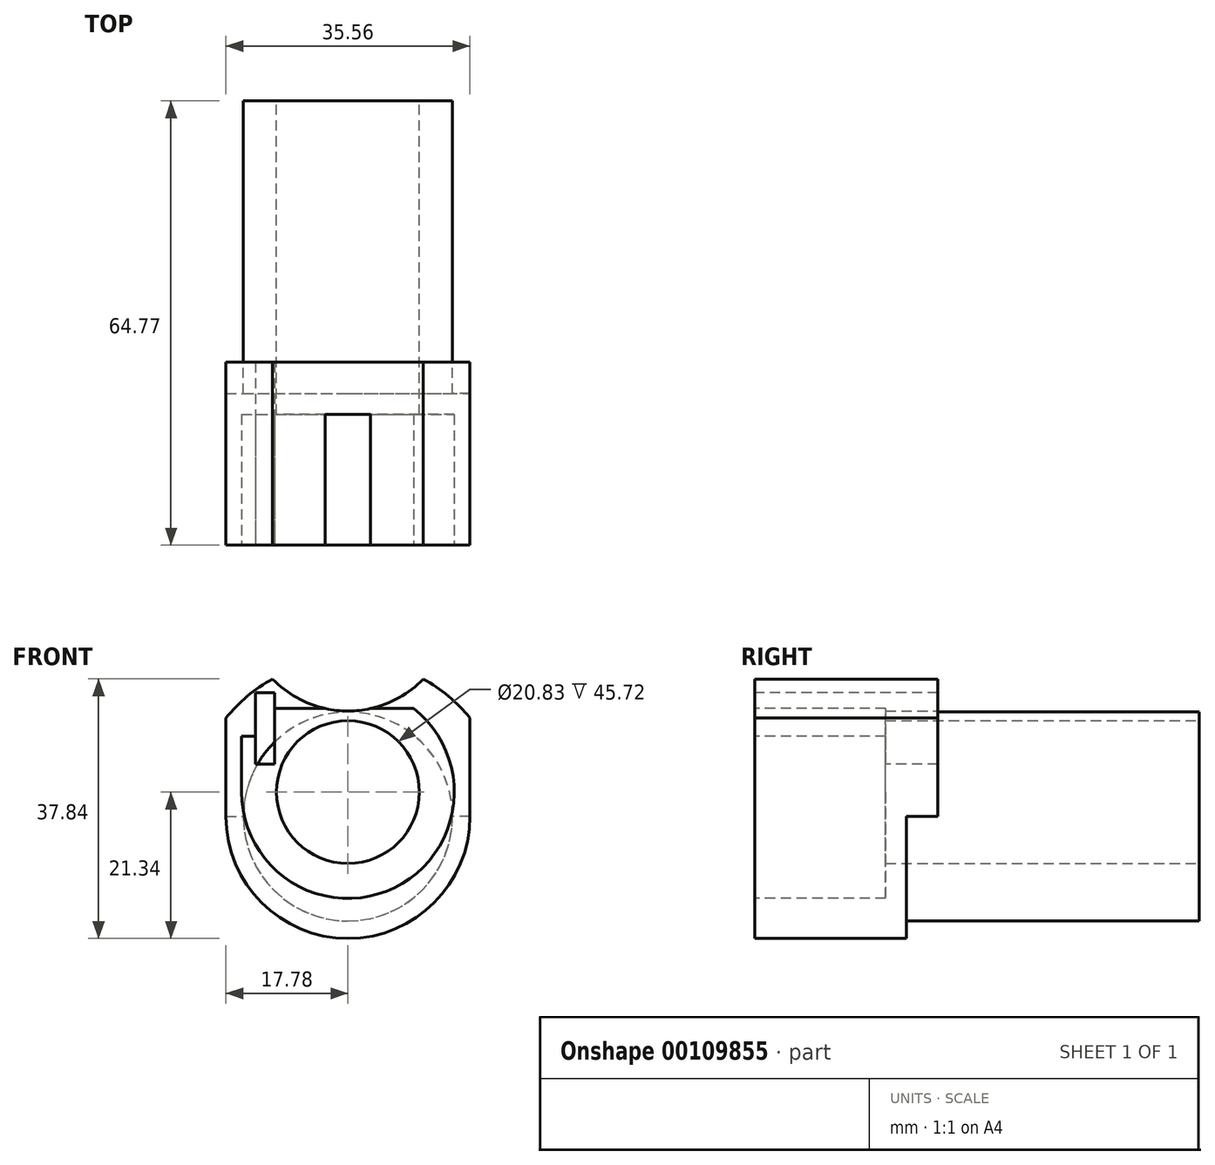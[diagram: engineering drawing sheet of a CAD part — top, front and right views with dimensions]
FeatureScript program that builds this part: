
annotation { "Feature Type Name" : "Feature", "Feature Type Description" : "" }
export const myFeature = defineFeature(function(context is Context, id is Id, definition is map)
    precondition{}
    {
        {
            var Q0;
            Q0=qCreatedBy(makeId("Front.planeOp"),FACE);
            var sketch = newSketch(context, id + "F0", { "sketchPlane" : qUnion([Q0])});
            skCircle(sketch, "E0", {"center": v(0, 0) * mm, "radius": 10.41 * mm});
            skCircle(sketch, "E1", {"center": v(0, -3.56) * mm, "radius": 15.24 * mm});
            skArc(sketch, "E2", {"start": v(-17.78, -3.56) * mm, "mid": v(0, -21.34) * mm, "end": v(17.78, -3.56) * mm});
            skLineSegment(sketch, "E3", {"start": v(-17.78, -3.56) * mm, "end": v(-17.78, 10.81) * mm});
            skLineSegment(sketch, "E4", {"start": v(17.78, 10.81) * mm, "end": v(17.78, -3.56) * mm});
            skArc(sketch, "E5", {"start": v(17.78, 10.81) * mm, "mid": v(14.66, 13.99) * mm, "end": v(10.98, 16.5) * mm});
            skArc(sketch, "E6.trimOffspring", {"start": v(-10.98, 16.5) * mm, "mid": v(-14.66, 13.99) * mm, "end": v(-17.78, 10.81) * mm});
            skArc(sketch, "E7", {"start": v(-10.98, 16.5) * mm, "mid": v(0, 11.83) * mm, "end": v(10.98, 16.5) * mm});
            skSolve(sketch);
        }
        {
            var Q0;
            Q0=makeQuery(id+"F0.imprint","IMPRINT",FACE,{"disambiguationData":[TD([[makeQuery(id+"F0.imprint","IMPRINT",EDGE,{"derivedFrom":sQuery(id+"F0.wireOp",EDGE,"E1")}),-1.0]])]});
            var Q1;
            Q1=makeQuery(id+"F0.imprint","IMPRINT",FACE,{"disambiguationData":[TD([[makeQuery(id+"F0.imprint","IMPRINT",EDGE,{"derivedFrom":sQuery(id+"F0.wireOp",EDGE,"E0")}),-1.0]])]});
            extrude(context, id + "F1", {"entities" : qUnion([Q0, Q1]), "depth" : 26.67 * mm});
        }
        {
            var Q0;
            Q0=makeQuery(id+"F0.imprint","IMPRINT",FACE,{"disambiguationData":[TD([[makeQuery(id+"F0.imprint","IMPRINT",EDGE,{"derivedFrom":sQuery(id+"F0.wireOp",EDGE,"E0")}),-1.0]])]});
            extrude(context, id + "F2", {"entities" : qUnion([Q0]), "operationType" : NewBodyOperationType.ADD, "oppositeDirection" : true, "depth" : 38.1 * mm});
        }
        {
            var Q0;
            Q0=makeQuery(id+"F1.opExtrude","CAP_FACE",FACE,{"disambiguationData":[OSD([sQuery(id+"F0.wireOp",EDGE,"E0"),sQuery(id+"F0.wireOp",EDGE,"E2"),sQuery(id+"F0.wireOp",EDGE,"E3"),sQuery(id+"F0.wireOp",EDGE,"IbQ5Rbc7-AV1b-1s0N-eDUH-5BoviFTMLuIW"),sQuery(id+"F0.wireOp",EDGE,"E4"),sQuery(id+"F0.wireOp",EDGE,"E5"),sQuery(id+"F0.wireOp",EDGE,"E6.trimOffspring"),sQuery(id+"F0.wireOp",EDGE,"E7"),sQuery(id+"F0.wireOp",EDGE,"53bd22bc-33cb-4a66-93e6-16bc93a2ea57.trimOffspring")])],"isStart":false});
            var sketch = newSketch(context, id + "F3", { "sketchPlane" : qUnion([Q0])});
            skArc(sketch, "E8", {"start": v(-15.5, 0) * mm, "mid": v(6.78, -13.93) * mm, "end": v(9.56, 12.2) * mm});
            skLineSegment(sketch, "E9", {"start": v(-15.5, 0) * mm, "end": v(-15.5, 8.13) * mm});
            skLineSegment(sketch, "E10", {"start": v(-10.67, 12.2) * mm, "end": v(9.56, 12.2) * mm});
            skLineSegment(sketch, "E11.bottom", {"start": v(-13.46, 14.48) * mm, "end": v(-10.67, 14.48) * mm});
            skLineSegment(sketch, "E11.top", {"start": v(-13.46, 4.06) * mm, "end": v(-10.67, 4.06) * mm});
            skLineSegment(sketch, "E11.left", {"start": v(-13.46, 14.48) * mm, "end": v(-13.46, 4.06) * mm});
            skLineSegment(sketch, "E11.right", {"start": v(-10.67, 14.48) * mm, "end": v(-10.67, 4.06) * mm});
            skLineSegment(sketch, "E12", {"start": v(-15.5, 8.13) * mm, "end": v(-13.46, 8.13) * mm});
            skSolve(sketch);
        }
        {
            var Q0;
            {var subQ3=sQuery(id+"F3.wireOp",EDGE,"E11.bottom");Q0=makeQuery(id+"F3.imprint","IMPRINT",FACE,{"disambiguationData":[TD([[makeQuery(id+"F3.imprint","IMPRINT",EDGE,{"derivedFrom":subQ3}),-1.0]])]});}
            extrude(context, id + "F4", {"entities" : qUnion([Q0]), "operationType" : NewBodyOperationType.REMOVE, "oppositeDirection" : true, "depth" : 26.67 * mm});
        }
        {
            var Q0;
            Q0=makeQuery(id+"F3.imprint","IMPRINT",FACE,{"disambiguationData":[TD([[makeQuery(id+"F3.imprint","IMPRINT",EDGE,{"derivedFrom":sQuery(id+"F3.wireOp",EDGE,"E8")}),1.0]])]});
            extrude(context, id + "F5", {"entities" : qUnion([Q0]), "operationType" : NewBodyOperationType.REMOVE, "oppositeDirection" : true, "depth" : 19.05 * mm});
        }
        {
            var Q0;
            Q0=makeQuery(id+"F1.opExtrude","CAP_FACE",FACE,{"disambiguationData":[OSD([sQuery(id+"F0.wireOp",EDGE,"E0"),sQuery(id+"F0.wireOp",EDGE,"E2"),sQuery(id+"F0.wireOp",EDGE,"E3"),sQuery(id+"F0.wireOp",EDGE,"IbQ5Rbc7-AV1b-1s0N-eDUH-5BoviFTMLuIW"),sQuery(id+"F0.wireOp",EDGE,"E4"),sQuery(id+"F0.wireOp",EDGE,"E5"),sQuery(id+"F0.wireOp",EDGE,"E6.trimOffspring"),sQuery(id+"F0.wireOp",EDGE,"E7"),sQuery(id+"F0.wireOp",EDGE,"53bd22bc-33cb-4a66-93e6-16bc93a2ea57.trimOffspring")])],"isStart":true});
            var sketch = newSketch(context, id + "F6", { "sketchPlane" : qUnion([Q0])});
            skLineSegment(sketch, "E13", {"start": v(-17.78, -3.56) * mm, "end": v(-15.24, -3.56) * mm});
            skLineSegment(sketch, "E14", {"start": v(17.78, -3.56) * mm, "end": v(15.24, -3.56) * mm});
            skSolve(sketch);
        }
        {
            var Q0;
            {var subQ0=sQuery(id+"F6.wireOp",EDGE,"E13");Q0=makeQuery(id+"F6.imprint","IMPRINT",FACE,{"disambiguationData":[TD([[makeQuery(id+"F6.imprint","IMPRINT",EDGE,{"derivedFrom":subQ0}),-1.0]])]});}
            extrude(context, id + "F7", {"entities" : qUnion([Q0]), "operationType" : NewBodyOperationType.REMOVE, "oppositeDirection" : true, "depth" : 4.57 * mm});
        }
    });
